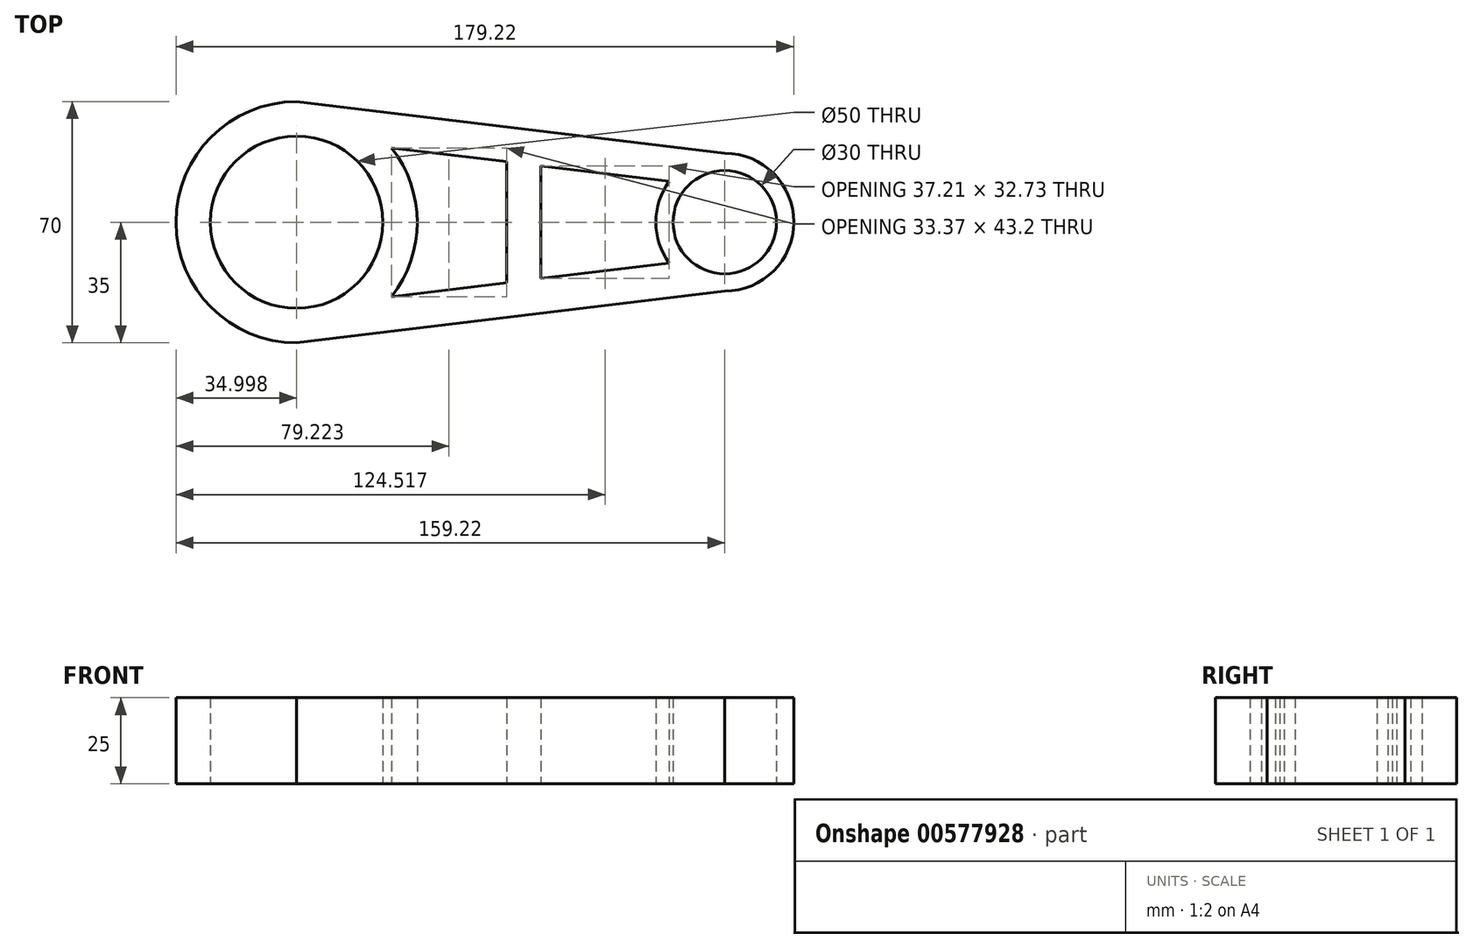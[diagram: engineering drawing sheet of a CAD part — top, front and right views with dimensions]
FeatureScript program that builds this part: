
annotation { "Feature Type Name" : "Feature", "Feature Type Description" : "" }
export const myFeature = defineFeature(function(context is Context, id is Id, definition is map)
    precondition{}
    {
        {
            var Q0;
            Q0=qCreatedBy(makeId("Top.planeOp"),FACE);
            var sketch = newSketch(context, id + "F0", { "sketchPlane" : qUnion([Q0])});
            skCircle(sketch, "E0", {"center": v(-71.55, 0) * mm, "radius": 25 * mm});
            skCircle(sketch, "E1", {"center": v(52.67, 0) * mm, "radius": 15 * mm});
            skLineSegment(sketch, "E2", {"start": v(-71.55, 35) * mm, "end": v(52.67, 20) * mm});
            skLineSegment(sketch, "E3", {"start": v(-71.55, -35) * mm, "end": v(52.67, -20) * mm});
            skLineSegment(sketch, "E4.0", {"start": v(-44.01, 21.6) * mm, "end": v(-10.64, 17.57) * mm});
            skLineSegment(sketch, "E5.0", {"start": v(-44.01, -21.6) * mm, "end": v(-10.64, -17.57) * mm});
            skArc(sketch, "E6", {"start": v(-44.01, 21.6) * mm, "mid": v(-36.55, 0) * mm, "end": v(-44.01, -21.6) * mm});
            skArc(sketch, "E7", {"start": v(36.57, 11.87) * mm, "mid": v(32.67, 0) * mm, "end": v(36.57, -11.87) * mm});
            skLineSegment(sketch, "E8", {"start": v(-10.64, 17.57) * mm, "end": v(-10.64, -17.57) * mm});
            skLineSegment(sketch, "E9", {"start": v(-0.64, 16.36) * mm, "end": v(-0.64, -16.36) * mm});
            skPoint(sketch, "E10.orphan", {"position": v(-72.75, 25.07) * mm});
            skPoint(sketch, "E11.orphan", {"position": v(-72.75, -25.07) * mm});
            skLineSegment(sketch, "E12.trimOffspring", {"start": v(-0.64, 16.36) * mm, "end": v(36.57, 11.87) * mm});
            skLineSegment(sketch, "E13.trimOffspring", {"start": v(-0.64, -16.36) * mm, "end": v(36.57, -11.87) * mm});
            skPoint(sketch, "E14.orphan", {"position": v(51.47, 10.07) * mm});
            skPoint(sketch, "E15.orphan", {"position": v(51.47, -10.07) * mm});
            skArc(sketch, "E16", {"start": v(52.67, -20) * mm, "mid": v(72.67, 0) * mm, "end": v(52.67, 20) * mm});
            skArc(sketch, "E17", {"start": v(-71.55, 35) * mm, "mid": v(-106.55, 0) * mm, "end": v(-71.55, -35) * mm});
            skSolve(sketch);
        }
        {
            var Q0;
            Q0 = qSketchRegion(id + "F0", true);
            extrude(context, id + "F1", {"entities" : qUnion([Q0]), "depth" : 25 * mm, "offsetDistance" : 25 * mm});
        }
    });
